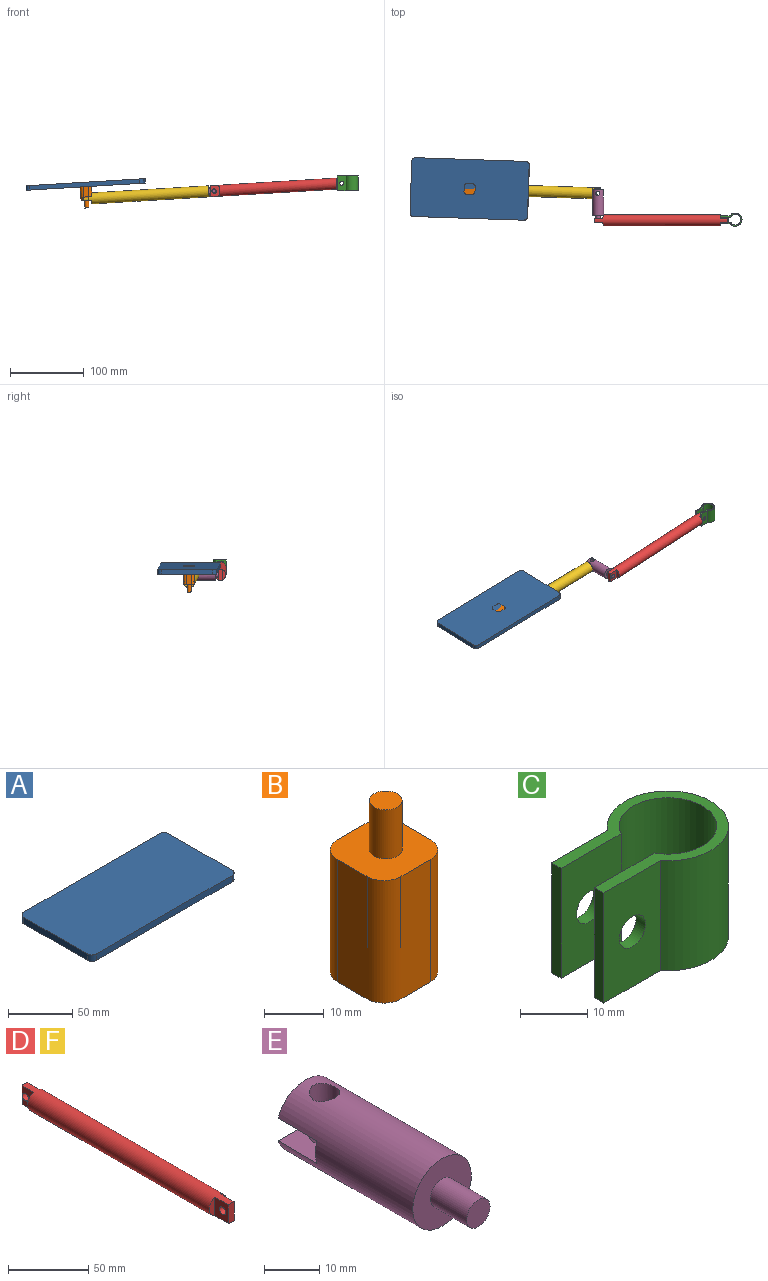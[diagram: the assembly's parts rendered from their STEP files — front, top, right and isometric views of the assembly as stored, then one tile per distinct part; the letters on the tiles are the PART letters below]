
ASSEMBLY  parts=6 mates=7
PART A: 10 faces, bbox 160x80x6.1 mm
  f0: plane 150x6.1mm, normal (0,1,0), area 915mm2, adj f4,f5,f6,f9
  f1: plane 70x6.1mm, normal (-1,0,0), area 427mm2, adj f4,f5,f6,f7
  f2: plane 150x6.1mm, normal (0,-1,0), area 915mm2, adj f4,f5,f7,f8
  f3: plane 70x6.1mm, normal (1,0,0), area 427mm2, adj f4,f5,f8,f9
  f4: plane 160x80mm, normal (0,0,1), area 12778.5mm2, adj f0,f1,f2,f3,f6,f7,f8,f9
  f5: plane 160x80mm, normal (0,0,-1), area 12778.5mm2, adj f0,f1,f2,f3,f6,f7,f8,f9
  f6: cylinder r=5mm len=6.1mm, axis (0,0,1), area 47.9mm2, adj f0,f1,f4,f5
  f7: cylinder r=5mm len=6.1mm, axis (0,0,-1), area 47.9mm2, adj f1,f2,f4,f5
  f8: cylinder r=5mm len=6.1mm, axis (0,0,1), area 47.9mm2, adj f2,f3,f4,f5
  f9: cylinder r=5mm len=6.1mm, axis (0,0,-1), area 47.9mm2, adj f0,f3,f4,f5
PART B: 12 faces, bbox 15x15x35 mm
  f0: cylinder r=2.75mm len=10mm, axis (0,0,-1), area 172.6mm2, adj f1,f7
  f1: plane 5.49x5.49mm, normal (0,0,1), area 23.7mm2, adj f0
  f2: plane 25x7mm, normal (0,1,0), area 175mm2, adj f6,f7,f8,f11
  f3: plane 25x7mm, normal (-1,0,0), area 175mm2, adj f6,f7,f8,f9
  f4: plane 25x7mm, normal (0,-1,0), area 175mm2, adj f6,f7,f9,f10
  f5: plane 25x7mm, normal (1,0,0), area 175mm2, adj f6,f7,f10,f11
  f6: plane 15x15mm, normal (0,0,-1), area 211.3mm2, adj f2,f3,f4,f5,f8,f9,f10,f11
  f7: plane 15x15mm, normal (0,0,1), area 187.6mm2, adj f0,f2,f3,f4,f5,f8,f9,f10
  f8: cylinder r=4mm len=25mm, axis (0,0,-1), area 157.1mm2, adj f2,f3,f6,f7
  f9: cylinder r=4mm len=25mm, axis (0,0,1), area 157.1mm2, adj f3,f4,f6,f7
  f10: cylinder r=4mm len=25mm, axis (0,0,-1), area 157.1mm2, adj f4,f5,f6,f7
  f11: cylinder r=4mm len=25mm, axis (0,0,1), area 157.1mm2, adj f2,f5,f6,f7
PART C: 12 faces, bbox 28x18x20 mm
  f0: plane 20x11.83mm, normal (0,1,0), area 212.9mm2, adj f1,f7,f8,f9,f11
  f1: plane 20x2mm, normal (-1,0,0), area 40mm2, adj f0,f2,f8,f9
  f2: plane 20x12.61mm, normal (0,-1,0), area 228.4mm2, adj f1,f3,f8,f9,f11
  f3: cylinder r=7.25mm len=20mm, axis (0,0,-1), area 765mm2, adj f2,f4,f8,f9
  f4: plane 20x12.61mm, normal (0,1,0), area 228.4mm2, adj f3,f5,f8,f9,f10
  f5: plane 20x2mm, normal (-1,0,0), area 40mm2, adj f4,f6,f8,f9
  f6: plane 20x11.83mm, normal (0,-1,0), area 212.9mm2, adj f5,f7,f8,f9,f10
  f7: cylinder r=9mm len=20mm, axis (0,0,-1), area 894.3mm2, adj f0,f6,f8,f9
  f8: plane 27.96x18mm, normal (0,0,1), area 121.4mm2, adj f0,f1,f2,f3,f4,f5,f6,f7
  f9: plane 27.96x18mm, normal (0,0,-1), area 121.4mm2, adj f0,f1,f2,f3,f4,f5,f6,f7
  f10: cylinder r=2.75mm len=5.5mm, axis (0,-1,0), area 34.6mm2, adj f4,f6
  f11: cylinder r=2.75mm len=5.5mm, axis (0,-1,0), area 34.6mm2, adj f0,f2
PART D: 13 faces, bbox 15x182x15 mm
  f0: plane 14.14x5mm, normal (0,-1,0), area 51.6mm2, adj f1,f4
  f1: cylinder r=7.5mm len=182mm, axis (0,1,0), area 7764.1mm2, adj f0,f2,f3,f4,f6,f7,f8,f9
  f2: plane 14.14x5mm, normal (0,-1,0), area 51.6mm2, adj f1,f3
  f3: plane 14.14x12mm, normal (-1,0,0), area 145.9mm2, adj f1,f2,f5,f12
  f4: plane 14.14x12mm, normal (1,0,0), area 145.9mm2, adj f0,f1,f5,f12
  f5: cylinder r=2.75mm len=5.5mm, axis (1,0,0), area 86.4mm2, adj f3,f4
  f6: plane 14.14x5mm, normal (0,1,0), area 51.6mm2, adj f1,f9
  f7: plane 14.14x5mm, normal (0,1,0), area 51.6mm2, adj f1,f8
  f8: plane 14.14x10mm, normal (-1,0,0), area 117.7mm2, adj f1,f7,f10,f11
  f9: plane 14.14x10mm, normal (1,0,0), area 117.7mm2, adj f1,f6,f10,f11
  f10: plane 15x5mm, normal (0,1,0), area 73.6mm2, adj f1,f8,f9
  f11: cylinder r=2.75mm len=5.5mm, axis (1,0,0), area 86.4mm2, adj f8,f9
  f12: plane 15x5mm, normal (0,-1,0), area 73.6mm2, adj f1,f3,f4
PART E: 11 faces, bbox 15x44.3x15 mm
  f0: cylinder r=7.5mm len=35mm, axis (0,1,0), area 1499mm2, adj f1,f2,f5,f6,f7,f8,f9,f10
  f1: plane 15x5mm, normal (0,1,0), area 73.6mm2, adj f0,f5,f7
  f2: plane 15x15mm, normal (0,-1,0), area 148.4mm2, adj f0,f3
  f3: cylinder r=3mm len=9.3mm, axis (0,1,0), area 175.3mm2, adj f2,f4
  f4: plane 6x6mm, normal (0,-1,0), area 28.3mm2, adj f3
  f5: plane 14.14x10mm, normal (0,0,-1), area 117.7mm2, adj f0,f1,f6,f9
  f6: plane 14.14x5mm, normal (0,1,0), area 51.6mm2, adj f0,f5
  f7: plane 14.14x10mm, normal (0,0,1), area 117.7mm2, adj f0,f1,f8,f10
  f8: plane 14.14x5mm, normal (0,1,0), area 51.6mm2, adj f0,f7
  f9: cylinder r=2.75mm len=5.5mm, axis (0,0,-1), area 81.9mm2, adj f0,f5
  f10: cylinder r=2.75mm len=5.5mm, axis (0,0,1), area 81.9mm2, adj f0,f7
PART F: same geometry as D
PLACE A rot(axis=(0.01,-0.87,-0.49),4deg) t=(-379.66,59.07,3.43)mm
PLACE B rot(axis=(0.02,1,0),176.5deg) t=(-366.06,41.22,-14.69)mm
PLACE C t=(-5.89,-0.43,-1.23)mm fixed
PLACE D rot(axis=(0.71,0.71,0.02),177.6deg) t=(-105.7,-1.43,3.53)mm
PLACE E rot(axis=(0,-1,0),3.5deg) t=(-192.54,30.37,-1.71)mm
PLACE F rot(axis=(-0.56,-0.58,-0.6),123.1deg) t=(-279.42,38.29,-6.95)mm
MATE revolute F.f11 <-> E.f9  axis (-0.06,0,1) through (-192.78,35.37,0.78)mm
MATE fastened B.f6 <-> A.f4  axis (-0.06,0,1) through (-367.33,41.37,10.28)mm
MATE pin_slot B.f0 <-> F.f5  axis (0.06,0,-1) through (-366.06,41.22,-14.69)mm
MATE pin_slot B.f0 <-> F.f5  axis (0.06,0,-1) through (-365.46,41.22,-24.67)mm
MATE pin_slot B.f0 <-> F.f5  axis (0.06,0,-1) through (-366.06,41.22,-14.69)mm
MATE fastened E.f3 <-> D.f5  axis (0,-1,0) through (-192.54,-3.93,-1.71)mm
MATE revolute D.f11 <-> C.f10  axis (0,-1,0) through (-18.85,-3.93,8.77)mm
